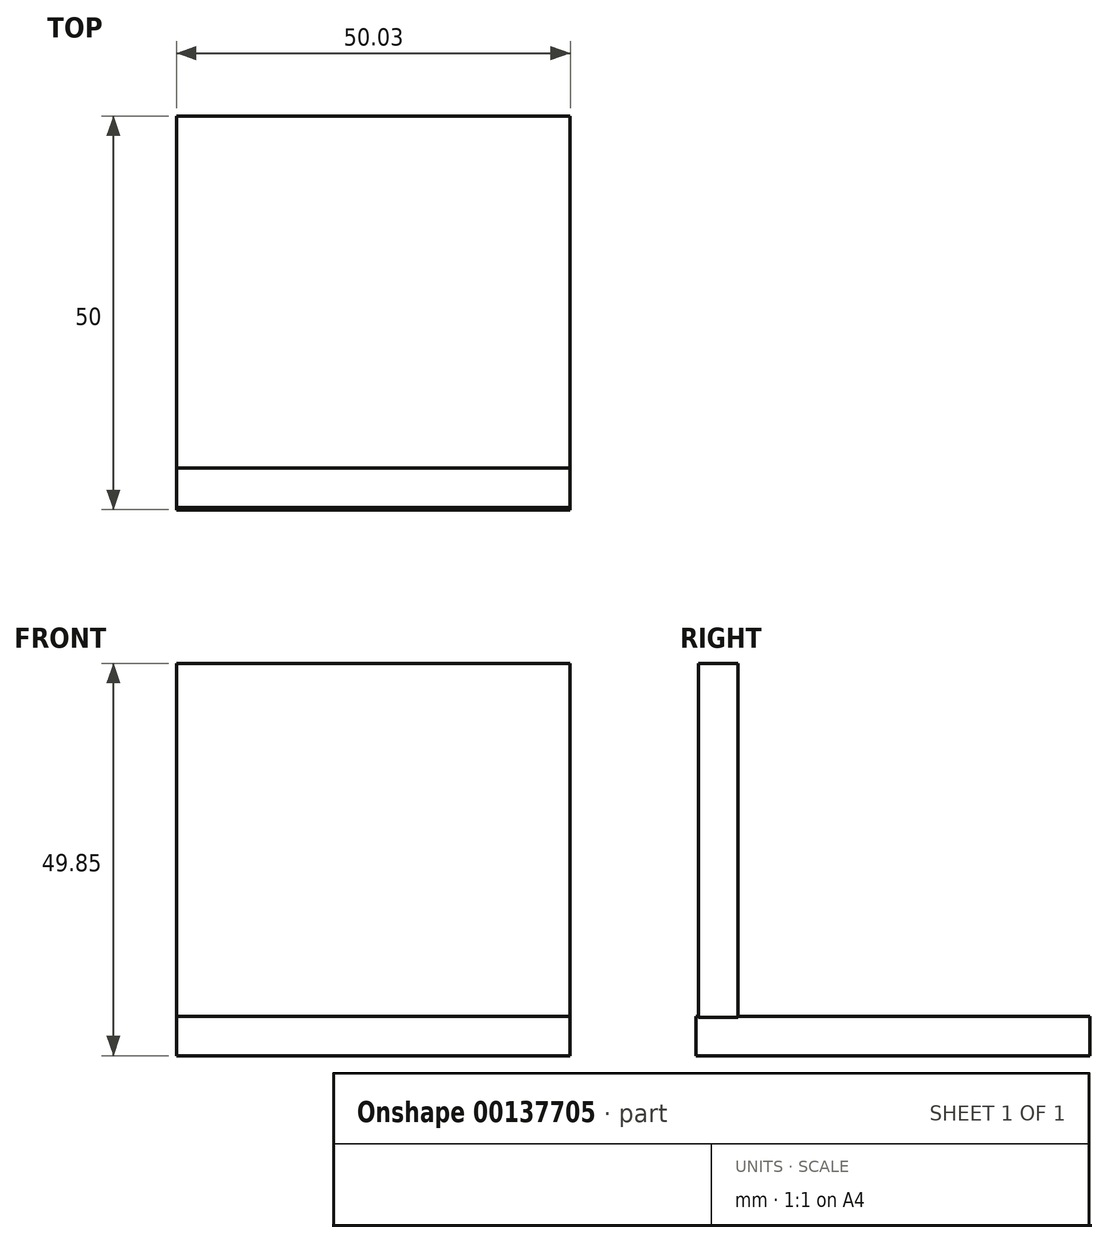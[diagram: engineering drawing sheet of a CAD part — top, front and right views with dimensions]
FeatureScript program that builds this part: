
annotation { "Feature Type Name" : "Feature", "Feature Type Description" : "" }
export const myFeature = defineFeature(function(context is Context, id is Id, definition is map)
    precondition{}
    {
        {
            var Q0;
            Q0=qCreatedBy(makeId("Top.planeOp"),FACE);
            var sketch = newSketch(context, id + "F0", { "sketchPlane" : qUnion([Q0])});
            skLineSegment(sketch, "E0", {"start": v(-22.07, 24.69) * mm, "end": v(27.93, 24.69) * mm});
            skLineSegment(sketch, "E1", {"start": v(27.93, 24.69) * mm, "end": v(27.93, -25.31) * mm});
            skLineSegment(sketch, "E2", {"start": v(27.93, -25.31) * mm, "end": v(-22.07, -25.31) * mm});
            skLineSegment(sketch, "E3", {"start": v(-22.07, -25.31) * mm, "end": v(-22.07, 24.69) * mm});
            skSolve(sketch);
        }
        {
            var Q0;
            Q0 = qSketchRegion(id + "F0", true);
            extrude(context, id + "F1", {"entities" : qUnion([Q0]), "depth" : 5 * mm});
        }
        {
            var Q0;
            Q0=qCreatedBy(makeId("Front.planeOp"),FACE);
            cPlane(context, id + "F2", {"entities" : qUnion([Q0]), "cplaneType" : CPlaneType.OFFSET, "offset" : 25 * mm, "width" : 150 * mm, "height" : 150 * mm});
        }
        {
            var Q0;
            Q0=qCreatedBy(id+"F2.planeOp",FACE);
            var sketch = newSketch(context, id + "F3", { "sketchPlane" : qUnion([Q0])});
            skLineSegment(sketch, "E4.bottom", {"start": v(-22.04, 4.85) * mm, "end": v(27.96, 4.85) * mm});
            skLineSegment(sketch, "E4.top", {"start": v(-22.04, 49.85) * mm, "end": v(27.96, 49.85) * mm});
            skLineSegment(sketch, "E4.left", {"start": v(-22.04, 4.85) * mm, "end": v(-22.04, 49.85) * mm});
            skLineSegment(sketch, "E4.right", {"start": v(27.96, 4.85) * mm, "end": v(27.96, 49.85) * mm});
            skSolve(sketch);
        }
        {
            var Q0;
            Q0 = qSketchRegion(id + "F3", true);
            extrude(context, id + "F4", {"entities" : qUnion([Q0]), "operationType" : NewBodyOperationType.ADD, "oppositeDirection" : true, "depth" : 5 * mm});
        }
    });
